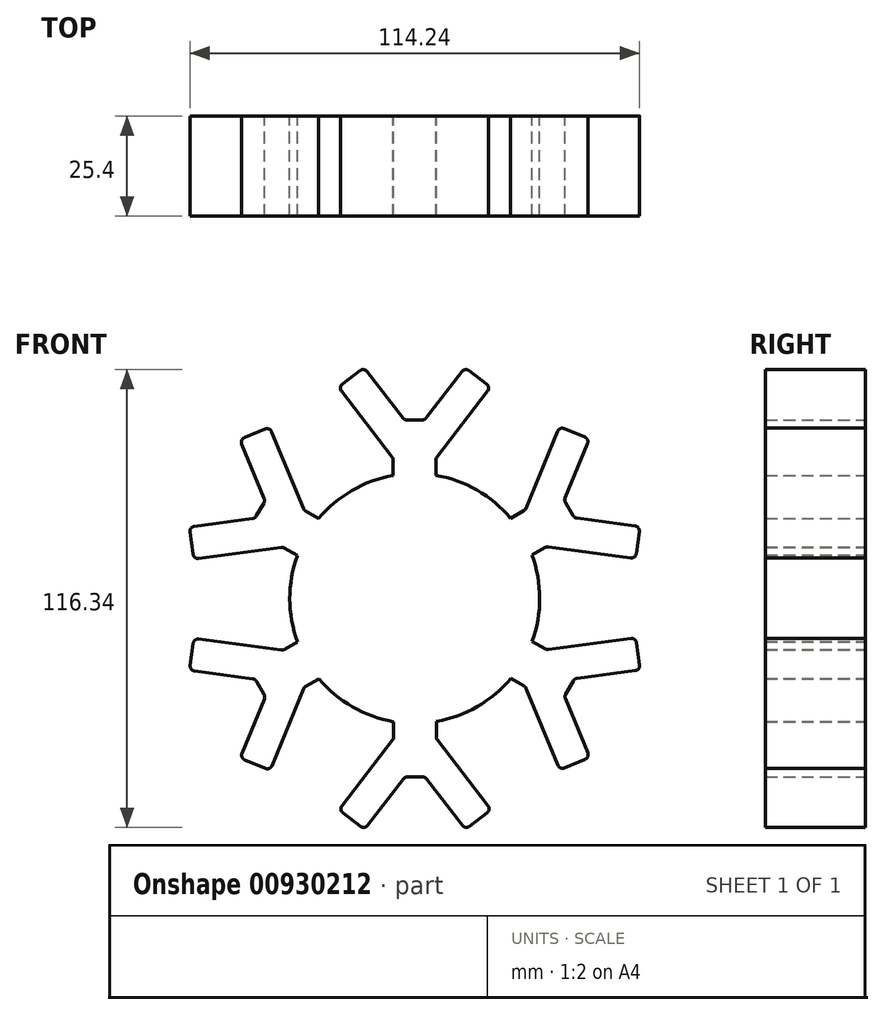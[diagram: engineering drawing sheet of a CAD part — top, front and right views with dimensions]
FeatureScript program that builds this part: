
annotation { "Feature Type Name" : "Feature", "Feature Type Description" : "" }
export const myFeature = defineFeature(function(context is Context, id is Id, definition is map)
    precondition{}
    {
        {
            var Q0;
            Q0=qCreatedBy(makeId("Front.planeOp"),FACE);
            var sketch = newSketch(context, id + "F0", { "sketchPlane" : qUnion([Q0])});
            skCircle(sketch, "E0", {"center": v(0, 0) * mm, "radius": 31.75 * mm});
            skLineSegment(sketch, "E1", {"start": v(5.38, 45.36) * mm, "end": v(5.35, 45.36) * mm});
            skLineSegment(sketch, "E2", {"start": v(-3.03, 45.85) * mm, "end": v(-12.14, 57.67) * mm});
            skLineSegment(sketch, "E3", {"start": v(-13.92, 57.9) * mm, "end": v(-18.41, 54.44) * mm});
            skLineSegment(sketch, "E4", {"start": v(-18.64, 52.66) * mm, "end": v(-5.74, 35.92) * mm});
            skLineSegment(sketch, "E5", {"start": v(-0.07, 45.36) * mm, "end": v(-0.07, 59.63) * mm});
            skLineSegment(sketch, "E6.MirrorCS", {"start": v(2.9, 45.85) * mm, "end": v(12, 57.67) * mm});
            skLineSegment(sketch, "E7.MirrorCS", {"start": v(13.78, 57.9) * mm, "end": v(18.28, 54.44) * mm});
            skLineSegment(sketch, "E8.MirrorCS", {"start": v(18.51, 52.66) * mm, "end": v(5.61, 35.92) * mm});
            skLineSegment(sketch, "E9.trimOffspring", {"start": v(1.9, 45.36) * mm, "end": v(-2.02, 45.36) * mm});
            skLineSegment(sketch, "E10", {"start": v(-5.48, 35.14) * mm, "end": v(-5.48, 31.27) * mm});
            skLineSegment(sketch, "E11", {"start": v(5.35, 35.14) * mm, "end": v(5.35, 31.3) * mm});
            skPoint(sketch, "E12.visualSharp", {"position": v(-12.91, 58.68) * mm});
            skArc(sketch, "E12.filletArc", {"start": v(-12.14, 57.67) * mm, "mid": v(-12.98, 58.16) * mm, "end": v(-13.92, 57.9) * mm});
            skPoint(sketch, "E13.visualSharp", {"position": v(-19.42, 53.66) * mm});
            skArc(sketch, "E13.filletArc", {"start": v(-18.41, 54.44) * mm, "mid": v(-18.9, 53.6) * mm, "end": v(-18.64, 52.66) * mm});
            skPoint(sketch, "E14.visualSharp", {"position": v(12.78, 58.68) * mm});
            skArc(sketch, "E14.filletArc", {"start": v(13.78, 57.9) * mm, "mid": v(12.85, 58.16) * mm, "end": v(12, 57.67) * mm});
            skPoint(sketch, "E15.visualSharp", {"position": v(19.29, 53.66) * mm});
            skArc(sketch, "E15.filletArc", {"start": v(18.51, 52.66) * mm, "mid": v(18.77, 53.6) * mm, "end": v(18.28, 54.44) * mm});
            skPoint(sketch, "E16.visualSharp", {"position": v(5.35, 35.57) * mm});
            skArc(sketch, "E16.filletArc", {"start": v(5.61, 35.92) * mm, "mid": v(5.42, 35.55) * mm, "end": v(5.35, 35.14) * mm});
            skPoint(sketch, "E17.visualSharp", {"position": v(-5.48, 35.57) * mm});
            skArc(sketch, "E17.filletArc", {"start": v(-5.48, 35.14) * mm, "mid": v(-5.55, 35.55) * mm, "end": v(-5.74, 35.92) * mm});
            skPoint(sketch, "E18.visualSharp", {"position": v(-2.65, 45.36) * mm});
            skArc(sketch, "E18.filletArc", {"start": v(-3.03, 45.85) * mm, "mid": v(-2.58, 45.5) * mm, "end": v(-2.02, 45.36) * mm});
            skPoint(sketch, "E19.visualSharp", {"position": v(2.52, 45.36) * mm});
            skArc(sketch, "E19.filletArc", {"start": v(1.9, 45.36) * mm, "mid": v(2.45, 45.5) * mm, "end": v(2.9, 45.85) * mm});
            skPoint(sketch, "E20.1.1", {"position": v(-38.03, 24.86) * mm});
            skPoint(sketch, "E20.1.2", {"position": v(-40.6, 20.39) * mm});
            skPoint(sketch, "E20.1.3", {"position": v(-33.55, 13.04) * mm});
            skPoint(sketch, "E20.1.4", {"position": v(-36.83, 43.54) * mm});
            skPoint(sketch, "E20.1.5", {"position": v(-44.43, 40.4) * mm});
            skLineSegment(sketch, "E20.1.6", {"start": v(-41.23, 20.3) * mm, "end": v(-56.02, 18.33) * mm});
            skPoint(sketch, "E20.1.7", {"position": v(-56.18, 10.01) * mm});
            skLineSegment(sketch, "E20.1.8", {"start": v(-54.93, 10.18) * mm, "end": v(-33.98, 12.98) * mm});
            skPoint(sketch, "E20.1.9", {"position": v(-57.27, 18.16) * mm});
            skLineSegment(sketch, "E20.1.10", {"start": v(-39.32, 22.62) * mm, "end": v(-51.67, 29.76) * mm});
            skLineSegment(sketch, "E20.1.11", {"start": v(-38.26, 25.44) * mm, "end": v(-43.95, 39.23) * mm});
            skPoint(sketch, "E20.1.12", {"position": v(-28.13, 22.42) * mm});
            skLineSegment(sketch, "E20.1.13", {"start": v(-43.25, 40.9) * mm, "end": v(-38, 43.05) * mm});
            skLineSegment(sketch, "E20.1.14", {"start": v(-36.35, 42.36) * mm, "end": v(-28.3, 22.82) * mm});
            skLineSegment(sketch, "E20.1.15", {"start": v(-57.1, 16.9) * mm, "end": v(-56.35, 11.27) * mm});
            skLineSegment(sketch, "E20.1.16", {"start": v(-38.34, 24.32) * mm, "end": v(-40.3, 20.93) * mm});
            skArc(sketch, "E20.1.17", {"start": v(-43.25, 40.9) * mm, "mid": v(-43.94, 40.2) * mm, "end": v(-43.95, 39.23) * mm});
            skArc(sketch, "E20.1.18", {"start": v(-36.35, 42.36) * mm, "mid": v(-37.03, 43.05) * mm, "end": v(-38, 43.05) * mm});
            skLineSegment(sketch, "E20.1.19", {"start": v(-36.6, 27.34) * mm, "end": v(-36.6, 27.31) * mm});
            skArc(sketch, "E20.1.20", {"start": v(-56.35, 11.27) * mm, "mid": v(-55.87, 10.43) * mm, "end": v(-54.93, 10.18) * mm});
            skArc(sketch, "E20.1.21", {"start": v(-38.34, 24.32) * mm, "mid": v(-38.17, 24.87) * mm, "end": v(-38.26, 25.44) * mm});
            skArc(sketch, "E20.1.22", {"start": v(-33.17, 12.82) * mm, "mid": v(-33.56, 12.97) * mm, "end": v(-33.98, 12.98) * mm});
            skArc(sketch, "E20.1.23", {"start": v(-28.3, 22.82) * mm, "mid": v(-28.08, 22.47) * mm, "end": v(-27.76, 22.2) * mm});
            skArc(sketch, "E20.1.24", {"start": v(-41.23, 20.3) * mm, "mid": v(-40.69, 20.5) * mm, "end": v(-40.3, 20.93) * mm});
            skArc(sketch, "E20.1.25", {"start": v(-56.02, 18.33) * mm, "mid": v(-56.86, 17.84) * mm, "end": v(-57.1, 16.9) * mm});
            skLineSegment(sketch, "E20.1.26", {"start": v(-27.76, 22.2) * mm, "end": v(-24.43, 20.28) * mm});
            skLineSegment(sketch, "E20.1.27", {"start": v(-33.17, 12.82) * mm, "end": v(-29.82, 10.9) * mm});
            skPoint(sketch, "E20.2.1", {"position": v(-40.54, -20.5) * mm});
            skPoint(sketch, "E20.2.2", {"position": v(-37.96, -24.97) * mm});
            skPoint(sketch, "E20.2.3", {"position": v(-28.07, -22.53) * mm});
            skPoint(sketch, "E20.2.4", {"position": v(-56.12, -10.13) * mm});
            skPoint(sketch, "E20.2.5", {"position": v(-57.2, -18.27) * mm});
            skLineSegment(sketch, "E20.2.6", {"start": v(-38.2, -25.55) * mm, "end": v(-43.88, -39.35) * mm});
            skPoint(sketch, "E20.2.7", {"position": v(-36.76, -43.65) * mm});
            skLineSegment(sketch, "E20.2.8", {"start": v(-36.28, -42.48) * mm, "end": v(-28.23, -22.93) * mm});
            skPoint(sketch, "E20.2.9", {"position": v(-44.36, -40.52) * mm});
            skLineSegment(sketch, "E20.2.10", {"start": v(-39.25, -22.74) * mm, "end": v(-51.6, -29.87) * mm});
            skLineSegment(sketch, "E20.2.11", {"start": v(-41.16, -20.42) * mm, "end": v(-55.95, -18.44) * mm});
            skPoint(sketch, "E20.2.12", {"position": v(-33.48, -13.16) * mm});
            skLineSegment(sketch, "E20.2.13", {"start": v(-57.04, -17.01) * mm, "end": v(-56.29, -11.39) * mm});
            skLineSegment(sketch, "E20.2.14", {"start": v(-54.86, -10.3) * mm, "end": v(-33.91, -13.1) * mm});
            skLineSegment(sketch, "E20.2.15", {"start": v(-43.19, -41) * mm, "end": v(-37.94, -43.17) * mm});
            skLineSegment(sketch, "E20.2.16", {"start": v(-40.23, -21.04) * mm, "end": v(-38.27, -24.43) * mm});
            skArc(sketch, "E20.2.17", {"start": v(-57.04, -17.01) * mm, "mid": v(-56.79, -17.95) * mm, "end": v(-55.95, -18.44) * mm});
            skArc(sketch, "E20.2.18", {"start": v(-54.86, -10.3) * mm, "mid": v(-55.8, -10.55) * mm, "end": v(-56.29, -11.39) * mm});
            skLineSegment(sketch, "E20.2.19", {"start": v(-41.97, -18.02) * mm, "end": v(-41.96, -18.05) * mm});
            skArc(sketch, "E20.2.20", {"start": v(-37.94, -43.17) * mm, "mid": v(-36.97, -43.16) * mm, "end": v(-36.28, -42.48) * mm});
            skArc(sketch, "E20.2.21", {"start": v(-40.23, -21.04) * mm, "mid": v(-40.62, -20.62) * mm, "end": v(-41.16, -20.42) * mm});
            skArc(sketch, "E20.2.22", {"start": v(-27.7, -22.32) * mm, "mid": v(-28.01, -22.58) * mm, "end": v(-28.23, -22.93) * mm});
            skArc(sketch, "E20.2.23", {"start": v(-33.91, -13.1) * mm, "mid": v(-33.5, -13.09) * mm, "end": v(-33.1, -12.94) * mm});
            skArc(sketch, "E20.2.24", {"start": v(-38.2, -25.55) * mm, "mid": v(-38.1, -24.98) * mm, "end": v(-38.27, -24.43) * mm});
            skArc(sketch, "E20.2.25", {"start": v(-43.88, -39.35) * mm, "mid": v(-43.88, -40.32) * mm, "end": v(-43.19, -41) * mm});
            skLineSegment(sketch, "E20.2.26", {"start": v(-33.1, -12.94) * mm, "end": v(-29.78, -11.02) * mm});
            skLineSegment(sketch, "E20.2.27", {"start": v(-27.7, -22.32) * mm, "end": v(-24.34, -20.38) * mm});
            skPoint(sketch, "E20.3.1", {"position": v(-2.52, -45.36) * mm});
            skPoint(sketch, "E20.3.2", {"position": v(2.65, -45.36) * mm});
            skPoint(sketch, "E20.3.3", {"position": v(5.48, -35.57) * mm});
            skPoint(sketch, "E20.3.4", {"position": v(-19.29, -53.66) * mm});
            skPoint(sketch, "E20.3.5", {"position": v(-12.78, -58.68) * mm});
            skLineSegment(sketch, "E20.3.6", {"start": v(3.03, -45.85) * mm, "end": v(12.14, -57.67) * mm});
            skPoint(sketch, "E20.3.7", {"position": v(19.42, -53.66) * mm});
            skLineSegment(sketch, "E20.3.8", {"start": v(18.64, -52.66) * mm, "end": v(5.74, -35.92) * mm});
            skPoint(sketch, "E20.3.9", {"position": v(12.91, -58.68) * mm});
            skLineSegment(sketch, "E20.3.10", {"start": v(0.07, -45.36) * mm, "end": v(0.07, -59.63) * mm});
            skLineSegment(sketch, "E20.3.11", {"start": v(-2.9, -45.85) * mm, "end": v(-12, -57.67) * mm});
            skPoint(sketch, "E20.3.12", {"position": v(-5.35, -35.57) * mm});
            skLineSegment(sketch, "E20.3.13", {"start": v(-13.78, -57.9) * mm, "end": v(-18.28, -54.44) * mm});
            skLineSegment(sketch, "E20.3.14", {"start": v(-18.51, -52.66) * mm, "end": v(-5.61, -35.92) * mm});
            skLineSegment(sketch, "E20.3.15", {"start": v(13.92, -57.9) * mm, "end": v(18.41, -54.44) * mm});
            skLineSegment(sketch, "E20.3.16", {"start": v(-1.9, -45.36) * mm, "end": v(2.02, -45.36) * mm});
            skArc(sketch, "E20.3.17", {"start": v(-13.78, -57.9) * mm, "mid": v(-12.85, -58.16) * mm, "end": v(-12, -57.67) * mm});
            skArc(sketch, "E20.3.18", {"start": v(-18.51, -52.66) * mm, "mid": v(-18.77, -53.6) * mm, "end": v(-18.28, -54.44) * mm});
            skLineSegment(sketch, "E20.3.19", {"start": v(-5.38, -45.36) * mm, "end": v(-5.35, -45.36) * mm});
            skArc(sketch, "E20.3.20", {"start": v(18.41, -54.44) * mm, "mid": v(18.9, -53.6) * mm, "end": v(18.64, -52.66) * mm});
            skArc(sketch, "E20.3.21", {"start": v(-1.9, -45.36) * mm, "mid": v(-2.45, -45.5) * mm, "end": v(-2.9, -45.85) * mm});
            skArc(sketch, "E20.3.22", {"start": v(5.48, -35.14) * mm, "mid": v(5.55, -35.55) * mm, "end": v(5.74, -35.92) * mm});
            skArc(sketch, "E20.3.23", {"start": v(-5.61, -35.92) * mm, "mid": v(-5.42, -35.55) * mm, "end": v(-5.35, -35.14) * mm});
            skArc(sketch, "E20.3.24", {"start": v(3.03, -45.85) * mm, "mid": v(2.58, -45.5) * mm, "end": v(2.02, -45.36) * mm});
            skArc(sketch, "E20.3.25", {"start": v(12.14, -57.67) * mm, "mid": v(12.98, -58.16) * mm, "end": v(13.92, -57.9) * mm});
            skLineSegment(sketch, "E20.3.26", {"start": v(-5.35, -35.14) * mm, "end": v(-5.35, -31.3) * mm});
            skLineSegment(sketch, "E20.3.27", {"start": v(5.48, -35.14) * mm, "end": v(5.48, -31.27) * mm});
            skPoint(sketch, "E20.4.1", {"position": v(38.03, -24.86) * mm});
            skPoint(sketch, "E20.4.2", {"position": v(40.6, -20.39) * mm});
            skPoint(sketch, "E20.4.3", {"position": v(33.55, -13.04) * mm});
            skPoint(sketch, "E20.4.4", {"position": v(36.83, -43.54) * mm});
            skPoint(sketch, "E20.4.5", {"position": v(44.43, -40.4) * mm});
            skLineSegment(sketch, "E20.4.6", {"start": v(41.23, -20.3) * mm, "end": v(56.02, -18.33) * mm});
            skPoint(sketch, "E20.4.7", {"position": v(56.18, -10.01) * mm});
            skLineSegment(sketch, "E20.4.8", {"start": v(54.93, -10.18) * mm, "end": v(33.98, -12.98) * mm});
            skPoint(sketch, "E20.4.9", {"position": v(57.27, -18.16) * mm});
            skLineSegment(sketch, "E20.4.10", {"start": v(39.32, -22.62) * mm, "end": v(51.67, -29.76) * mm});
            skLineSegment(sketch, "E20.4.11", {"start": v(38.26, -25.44) * mm, "end": v(43.95, -39.23) * mm});
            skPoint(sketch, "E20.4.12", {"position": v(28.13, -22.42) * mm});
            skLineSegment(sketch, "E20.4.13", {"start": v(43.25, -40.9) * mm, "end": v(38, -43.05) * mm});
            skLineSegment(sketch, "E20.4.14", {"start": v(36.35, -42.36) * mm, "end": v(28.3, -22.82) * mm});
            skLineSegment(sketch, "E20.4.15", {"start": v(57.1, -16.9) * mm, "end": v(56.35, -11.27) * mm});
            skLineSegment(sketch, "E20.4.16", {"start": v(38.34, -24.32) * mm, "end": v(40.3, -20.93) * mm});
            skArc(sketch, "E20.4.17", {"start": v(43.25, -40.9) * mm, "mid": v(43.94, -40.2) * mm, "end": v(43.95, -39.23) * mm});
            skArc(sketch, "E20.4.18", {"start": v(36.35, -42.36) * mm, "mid": v(37.03, -43.05) * mm, "end": v(38, -43.05) * mm});
            skLineSegment(sketch, "E20.4.19", {"start": v(36.6, -27.34) * mm, "end": v(36.6, -27.31) * mm});
            skArc(sketch, "E20.4.20", {"start": v(56.35, -11.27) * mm, "mid": v(55.87, -10.43) * mm, "end": v(54.93, -10.18) * mm});
            skArc(sketch, "E20.4.21", {"start": v(38.34, -24.32) * mm, "mid": v(38.17, -24.87) * mm, "end": v(38.26, -25.44) * mm});
            skArc(sketch, "E20.4.22", {"start": v(33.17, -12.82) * mm, "mid": v(33.56, -12.97) * mm, "end": v(33.98, -12.98) * mm});
            skArc(sketch, "E20.4.23", {"start": v(28.3, -22.82) * mm, "mid": v(28.08, -22.47) * mm, "end": v(27.76, -22.2) * mm});
            skArc(sketch, "E20.4.24", {"start": v(41.23, -20.3) * mm, "mid": v(40.69, -20.5) * mm, "end": v(40.3, -20.93) * mm});
            skArc(sketch, "E20.4.25", {"start": v(56.02, -18.33) * mm, "mid": v(56.86, -17.84) * mm, "end": v(57.1, -16.9) * mm});
            skLineSegment(sketch, "E20.4.26", {"start": v(27.76, -22.2) * mm, "end": v(24.43, -20.28) * mm});
            skLineSegment(sketch, "E20.4.27", {"start": v(33.17, -12.82) * mm, "end": v(29.82, -10.9) * mm});
            skPoint(sketch, "E20.5.1", {"position": v(40.54, 20.5) * mm});
            skPoint(sketch, "E20.5.2", {"position": v(37.96, 24.97) * mm});
            skPoint(sketch, "E20.5.3", {"position": v(28.07, 22.53) * mm});
            skPoint(sketch, "E20.5.4", {"position": v(56.12, 10.13) * mm});
            skPoint(sketch, "E20.5.5", {"position": v(57.2, 18.27) * mm});
            skLineSegment(sketch, "E20.5.6", {"start": v(38.2, 25.55) * mm, "end": v(43.88, 39.35) * mm});
            skPoint(sketch, "E20.5.7", {"position": v(36.76, 43.65) * mm});
            skLineSegment(sketch, "E20.5.8", {"start": v(36.28, 42.48) * mm, "end": v(28.23, 22.93) * mm});
            skPoint(sketch, "E20.5.9", {"position": v(44.36, 40.52) * mm});
            skLineSegment(sketch, "E20.5.10", {"start": v(39.25, 22.74) * mm, "end": v(51.6, 29.87) * mm});
            skLineSegment(sketch, "E20.5.11", {"start": v(41.16, 20.42) * mm, "end": v(55.95, 18.44) * mm});
            skPoint(sketch, "E20.5.12", {"position": v(33.48, 13.16) * mm});
            skLineSegment(sketch, "E20.5.13", {"start": v(57.04, 17.01) * mm, "end": v(56.29, 11.39) * mm});
            skLineSegment(sketch, "E20.5.14", {"start": v(54.86, 10.3) * mm, "end": v(33.91, 13.1) * mm});
            skLineSegment(sketch, "E20.5.15", {"start": v(43.19, 41) * mm, "end": v(37.94, 43.17) * mm});
            skLineSegment(sketch, "E20.5.16", {"start": v(40.23, 21.04) * mm, "end": v(38.27, 24.43) * mm});
            skArc(sketch, "E20.5.17", {"start": v(57.04, 17.01) * mm, "mid": v(56.79, 17.95) * mm, "end": v(55.95, 18.44) * mm});
            skArc(sketch, "E20.5.18", {"start": v(54.86, 10.3) * mm, "mid": v(55.8, 10.55) * mm, "end": v(56.29, 11.39) * mm});
            skLineSegment(sketch, "E20.5.19", {"start": v(41.97, 18.02) * mm, "end": v(41.96, 18.05) * mm});
            skArc(sketch, "E20.5.20", {"start": v(37.94, 43.17) * mm, "mid": v(36.97, 43.16) * mm, "end": v(36.28, 42.48) * mm});
            skArc(sketch, "E20.5.21", {"start": v(40.23, 21.04) * mm, "mid": v(40.62, 20.62) * mm, "end": v(41.16, 20.42) * mm});
            skArc(sketch, "E20.5.22", {"start": v(27.7, 22.32) * mm, "mid": v(28.01, 22.58) * mm, "end": v(28.23, 22.93) * mm});
            skArc(sketch, "E20.5.23", {"start": v(33.91, 13.1) * mm, "mid": v(33.5, 13.09) * mm, "end": v(33.1, 12.94) * mm});
            skArc(sketch, "E20.5.24", {"start": v(38.2, 25.55) * mm, "mid": v(38.1, 24.98) * mm, "end": v(38.27, 24.43) * mm});
            skArc(sketch, "E20.5.25", {"start": v(43.88, 39.35) * mm, "mid": v(43.88, 40.32) * mm, "end": v(43.19, 41) * mm});
            skLineSegment(sketch, "E20.5.26", {"start": v(33.1, 12.94) * mm, "end": v(29.78, 11.02) * mm});
            skLineSegment(sketch, "E20.5.27", {"start": v(27.7, 22.32) * mm, "end": v(24.34, 20.38) * mm});
            skSolve(sketch);
        }
        {
            var Q0;
            {var subQ0=sQuery(id+"F0.wireOp",EDGE,"E0");var subQ5=makeQuery(id+"F0.imprint","INTERSECT",VERTEX,{"derivedFrom":[subQ0,sQuery(id+"F0.wireOp",EDGE,"0d80c050-f1ba-42e5-aed5-5e658a0334f0.4.1")]});Q0=makeQuery(id+"F0.imprint","IMPRINT",FACE,{"disambiguationData":[TD([[makeQuery(id+"F0.imprint","IMPRINT",EDGE,{"disambiguationData":[TD([[subQ5,-1.0]])],"derivedFrom":subQ0}),1.0]])]});}
            var Q1;
            {var subQ0=sQuery(id+"F0.wireOp",EDGE,"E0");var subQ8=makeQuery(id+"F0.imprint","INTERSECT",VERTEX,{"derivedFrom":[sQuery(id+"F0.wireOp",EDGE,"E20.4.26"),subQ0]});Q1=makeQuery(id+"F0.imprint","IMPRINT",FACE,{"disambiguationData":[TD([[makeQuery(id+"F0.imprint","IMPRINT",EDGE,{"disambiguationData":[TD([[subQ8,-1.0]])],"derivedFrom":subQ0}),1.0]])]});}
            var Q2;
            Q2=makeQuery(id+"F0.imprint","IMPRINT",FACE,{"disambiguationData":[TD([[makeQuery(id+"F0.imprint","IMPRINT",EDGE,{"derivedFrom":sQuery(id+"F0.wireOp",EDGE,"E20.1.6")}),1.0]])]});
            var Q3;
            Q3=makeQuery(id+"F0.imprint","IMPRINT",FACE,{"disambiguationData":[TD([[makeQuery(id+"F0.imprint","IMPRINT",EDGE,{"derivedFrom":sQuery(id+"F0.wireOp",EDGE,"E2")}),1.0]])]});
            var Q4;
            Q4=makeQuery(id+"F0.imprint","IMPRINT",FACE,{"disambiguationData":[TD([[makeQuery(id+"F0.imprint","IMPRINT",EDGE,{"derivedFrom":sQuery(id+"F0.wireOp",EDGE,"E20.5.6")}),1.0]])]});
            var Q5;
            Q5=makeQuery(id+"F0.imprint","IMPRINT",FACE,{"disambiguationData":[TD([[makeQuery(id+"F0.imprint","IMPRINT",EDGE,{"derivedFrom":sQuery(id+"F0.wireOp",EDGE,"E20.4.6")}),1.0]])]});
            var Q6;
            Q6=makeQuery(id+"F0.imprint","IMPRINT",FACE,{"disambiguationData":[TD([[makeQuery(id+"F0.imprint","IMPRINT",EDGE,{"derivedFrom":sQuery(id+"F0.wireOp",EDGE,"E20.3.6")}),1.0]])]});
            var Q7;
            Q7=makeQuery(id+"F0.imprint","IMPRINT",FACE,{"disambiguationData":[TD([[makeQuery(id+"F0.imprint","IMPRINT",EDGE,{"derivedFrom":sQuery(id+"F0.wireOp",EDGE,"E20.2.6")}),1.0]])]});
            extrude(context, id + "F1", {"entities" : qUnion([Q0, Q1, Q2, Q3, Q4, Q5, Q6, Q7]), "depth" : 25.4 * mm, "offsetDistance" : 25.4 * mm});
        }
    });
